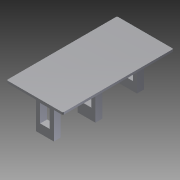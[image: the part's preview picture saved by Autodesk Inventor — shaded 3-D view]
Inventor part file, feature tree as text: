
AUTODESK INVENTOR PART (.ipt)
format: ipt  version: 2014 (Build 180170000, 170)  size: 124,928 bytes
history: native  units: in
note: dims shown in document units (in); Inventor stores cm internally (conversion verified against a paired STEP export)
features: other x7, extrude x3, sketch x3, pattern_linear x1
ambient origin geometry x8: Origin, YZ Plane, XZ Plane, XY Plane, X Axis, Y Axis, Z Axis, Center Point
bodies: Solid1 (feature_tree)
feature tree (14):
  extrude  "Extrusion1"  Depth=0.031in TaperAngle=0.0deg
  extrude  "Extrusion2"  Depth=0.031in TaperAngle=0.0deg
  pattern_linear  "Rectangular Pattern1"  [2 undecoded]
  extrude  "Extrusion3"  [1 undecoded]
  other  "to_base_XY"
  other  "to_base_YZ"
  other  "to_base_ZX"
  other  "to_base_X"
  other  "to_base_Y"
  other  "to_base_Z"
  other  "to_base_Center"
  sketch  "Sketch_2"  dims[d4=0.7874in d6=0.37in d7=0.3937in d9=0.0in d10=0.031in d11=0.0in]
  sketch  "Sketch_1"  dims[d0=0.01in d1=0.0in d2=0.031in d3=0.0in]
  sketch  "Sketch_14"
note: 3 required parameter values undecoded (feature->parameter linkage not recoverable at this tier; creation-order binding heuristic only, values carry confidence <= 0.55)
